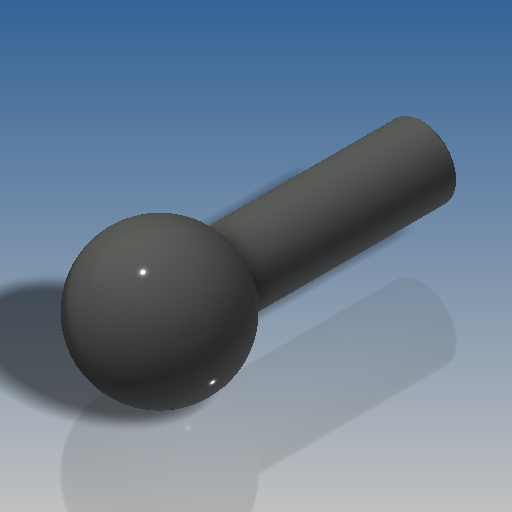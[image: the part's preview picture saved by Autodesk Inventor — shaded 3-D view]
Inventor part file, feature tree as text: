
AUTODESK INVENTOR PART (.ipt)
format: ipt  version: 2018.3 (Build 223284000, 284)  size: 180,224 bytes
history: native  units: in
note: dims shown in document units (in); Inventor stores cm internally (conversion verified against a paired STEP export)
features: revolve x1, fillet x1, sketch x1
ambient origin geometry x8: Origin, YZ Plane, XZ Plane, XY Plane, X Axis, Y Axis, Z Axis, Center Point
bodies: Solid1 (feature_tree)
feature tree (3):
  revolve  "Revolution1"  [1 undecoded]
  fillet  "Fillet1"  Radius=0.252in
  sketch  "Sketch2"  dims[d0=0.4724in d1=0.126in d2=0.252in d3=90.0deg d4=0.0039in]
note: 1 required parameter value undecoded (feature->parameter linkage not recoverable at this tier; creation-order binding heuristic only, values carry confidence <= 0.55)
